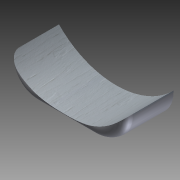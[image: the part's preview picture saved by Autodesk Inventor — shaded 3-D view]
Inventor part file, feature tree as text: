
AUTODESK INVENTOR PART (.ipt)
format: ipt  version: 2011 SP1 (Build 150282100, 282)  size: 123,392 bytes
history: native  units: in
note: dims shown in document units (in); Inventor stores cm internally (conversion verified against a paired STEP export)
features: other x3, fillet x2
ambient origin geometry x8: Origin, YZ Plane, XZ Plane, XY Plane, X Axis, Y Axis, Z Axis, Center Point
bodies: Solid1 (feature_tree)
feature tree (5):
  other  "Duct_Support.ipt"
  fillet  "Fillet1"  Radius=0.3937in
  fillet  "Fillet2"  Radius=1.5in
  other  "Solid1::Duct_Support.ipt"
  other  "TaggingFeature1"
